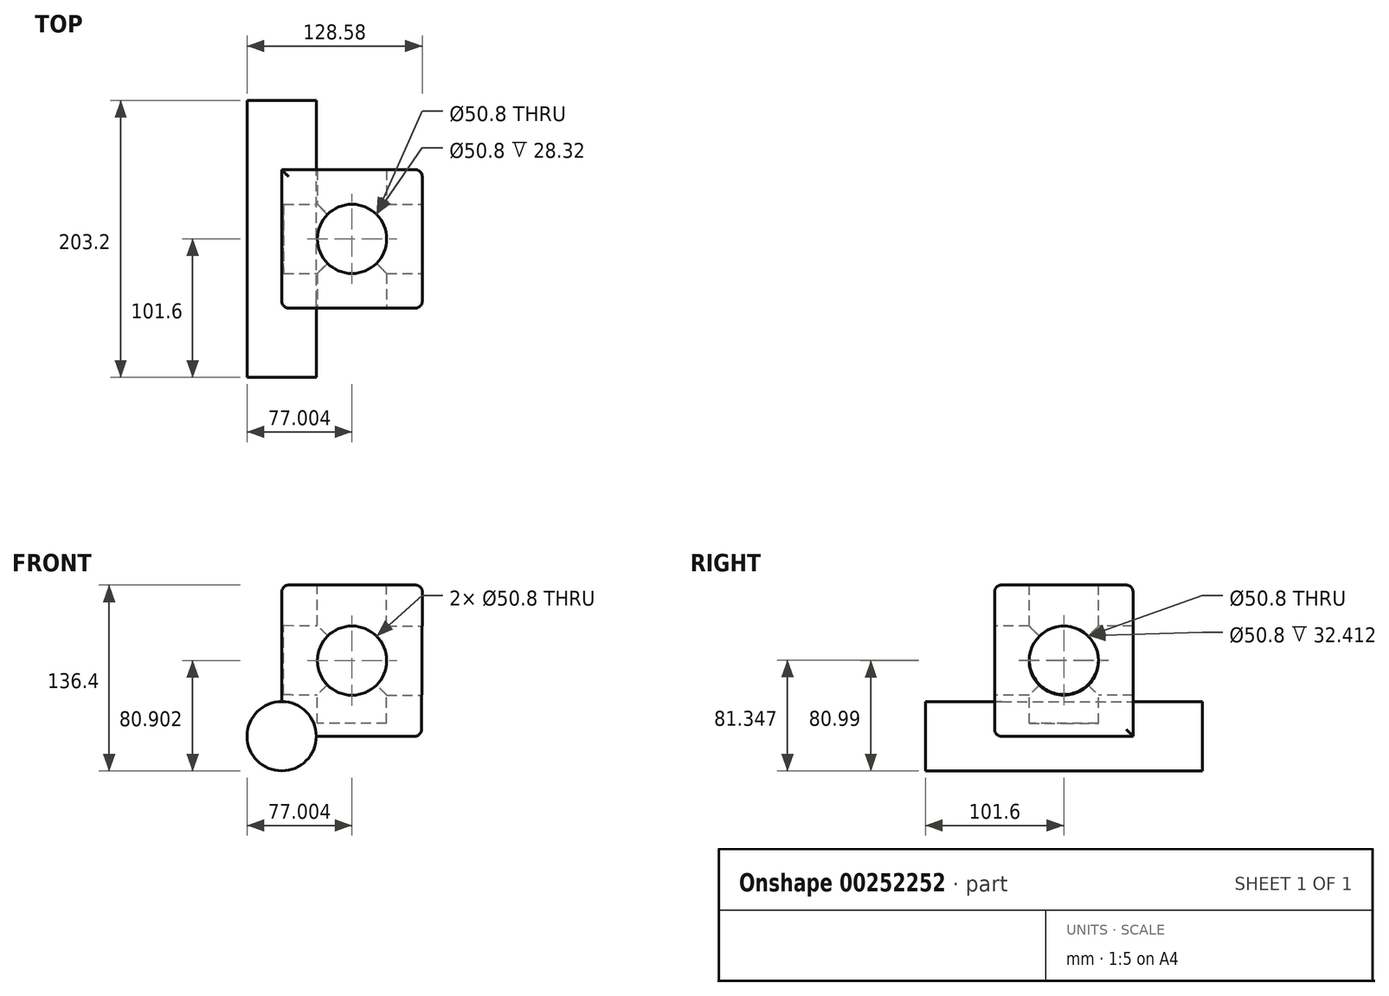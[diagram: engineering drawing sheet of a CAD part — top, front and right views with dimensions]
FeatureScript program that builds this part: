
annotation { "Feature Type Name" : "Feature", "Feature Type Description" : "" }
export const myFeature = defineFeature(function(context is Context, id is Id, definition is map)
    precondition{}
    {
        {
            var Q0;
            Q0=qCreatedBy(makeId("Front.planeOp"),FACE);
            var sketch = newSketch(context, id + "F0", { "sketchPlane" : qUnion([Q0])});
            skLineSegment(sketch, "E0", {"start": v(0, 0) * mm, "end": v(102.63, 0) * mm});
            skLineSegment(sketch, "E1", {"start": v(0, 0) * mm, "end": v(0, 111) * mm});
            skLineSegment(sketch, "E2", {"start": v(0, 111) * mm, "end": v(103.2, 111) * mm});
            skLineSegment(sketch, "E3", {"start": v(103.2, 111) * mm, "end": v(102.63, 0) * mm});
            skSolve(sketch);
        }
        {
            var Q0;
            Q0=makeQuery(id+"F0.imprint","IMPRINT",FACE,{"disambiguationData":[TD([[makeQuery(id+"F0.imprint","IMPRINT",EDGE,{"derivedFrom":sQuery(id+"F0.wireOp",EDGE,"E0")}),1.0]])]});
            extrude(context, id + "F1", {"entities" : qUnion([Q0]), "depth" : 101.6 * mm});
        }
        {
            var Q0;
            Q0=makeQuery(id+"F1.opExtrude","SWEPT_FACE",FACE,{"disambiguationData":[OSD([sQuery(id+"F0.wireOp",EDGE,"E2")])]});
            var sketch = newSketch(context, id + "F2", { "sketchPlane" : qUnion([Q0])});
            skPoint(sketch, "E4.start.orphan", {"position": v(51.6, 0) * mm});
            skCircle(sketch, "E5", {"center": v(51.6, -50.8) * mm, "radius": 25.4 * mm});
            skPoint(sketch, "E6.end.orphan", {"position": v(51.6, -101.6) * mm});
            skSolve(sketch);
        }
        {
            var Q0;
            Q0=makeQuery(id+"F2.imprint","IMPRINT",FACE,{"disambiguationData":[TD([[makeQuery(id+"F2.imprint","IMPRINT",EDGE,{"derivedFrom":sQuery(id+"F2.wireOp",EDGE,"E5")}),1.0]])]});
            extrude(context, id + "F3", {"entities" : qUnion([Q0]), "operationType" : NewBodyOperationType.REMOVE, "oppositeDirection" : true, "depth" : 101.6 * mm});
        }
        {
            var Q0;
            Q0=makeQuery(id+"F1.opExtrude","SWEPT_FACE",FACE,{"disambiguationData":[OSD([sQuery(id+"F0.wireOp",EDGE,"E3")])]});
            var sketch = newSketch(context, id + "F4", { "sketchPlane" : qUnion([Q0])});
            skCircle(sketch, "E7", {"center": v(-50.8, 56.04) * mm, "radius": 25.4 * mm});
            skPoint(sketch, "E8.orphan", {"position": v(-50.8, 111.54) * mm});
            skPoint(sketch, "E9.end.orphan", {"position": v(-50.8, 0.53) * mm});
            skSolve(sketch);
        }
        {
            var Q0;
            Q0=makeQuery(id+"F4.imprint","IMPRINT",FACE,{"disambiguationData":[TD([[makeQuery(id+"F4.imprint","IMPRINT",EDGE,{"derivedFrom":sQuery(id+"F4.wireOp",EDGE,"E7")}),1.0]])]});
            extrude(context, id + "F5", {"entities" : qUnion([Q0]), "operationType" : NewBodyOperationType.REMOVE, "oppositeDirection" : true, "depth" : 101.6 * mm});
        }
        {
            var Q0;
            Q0=makeQuery(id+"F1.opExtrude","CAP_FACE",FACE,{"disambiguationData":[OSD([sQuery(id+"F0.wireOp",EDGE,"E0"),sQuery(id+"F0.wireOp",EDGE,"E1"),sQuery(id+"F0.wireOp",EDGE,"E2"),sQuery(id+"F0.wireOp",EDGE,"E3")])],"isStart":false});
            var sketch = newSketch(context, id + "F6", { "sketchPlane" : qUnion([Q0])});
            skPoint(sketch, "E10.endSnap0", {"position": v(51.31, 0) * mm});
            skCircle(sketch, "E11", {"center": v(51.6, 55.5) * mm, "radius": 25.4 * mm});
            skPoint(sketch, "E12.orphan", {"position": v(51.6, 111) * mm});
            skPoint(sketch, "E10.end.orphan", {"position": v(51.6, 0) * mm});
            skSolve(sketch);
        }
        {
            var Q0;
            Q0=makeQuery(id+"F6.imprint","IMPRINT",FACE,{"disambiguationData":[TD([[makeQuery(id+"F6.imprint","IMPRINT",EDGE,{"derivedFrom":sQuery(id+"F6.wireOp",EDGE,"E11")}),1.0]])]});
            extrude(context, id + "F7", {"entities" : qUnion([Q0]), "operationType" : NewBodyOperationType.REMOVE, "oppositeDirection" : true, "depth" : 101.6 * mm});
        }
        {
            var Q0;
            Q0=makeQuery(id+"F1.opExtrude","SWEPT_EDGE",EDGE,{"disambiguationData":[OSD([sQuery(id+"F0.wireOp",EDGE,"E1"),sQuery(id+"F0.wireOp",EDGE,"E2")])]});
            var Q1;
            Q1=makeQuery(id+"F1.opExtrude","CAP_EDGE",EDGE,{"disambiguationData":[OSD([sQuery(id+"F0.wireOp",EDGE,"E2")])],"isStart":false});
            var Q2;
            Q2=makeQuery(id+"F1.opExtrude","SWEPT_EDGE",EDGE,{"disambiguationData":[OSD([sQuery(id+"F0.wireOp",EDGE,"E2"),sQuery(id+"F0.wireOp",EDGE,"E3")])]});
            var Q3;
            Q3=makeQuery(id+"F1.opExtrude","CAP_EDGE",EDGE,{"disambiguationData":[OSD([sQuery(id+"F0.wireOp",EDGE,"E2")])],"isStart":true});
            var Q4;
            Q4=makeQuery(id+"F1.opExtrude","CAP_EDGE",EDGE,{"disambiguationData":[OSD([sQuery(id+"F0.wireOp",EDGE,"E3")])],"isStart":true});
            var Q5;
            Q5=makeQuery(id+"F1.opExtrude","CAP_EDGE",EDGE,{"disambiguationData":[OSD([sQuery(id+"F0.wireOp",EDGE,"E3")])],"isStart":false});
            var Q6;
            Q6=makeQuery(id+"F1.opExtrude","SWEPT_EDGE",EDGE,{"disambiguationData":[OSD([sQuery(id+"F0.wireOp",EDGE,"E0"),sQuery(id+"F0.wireOp",EDGE,"E3")])]});
            var Q7;
            Q7=makeQuery(id+"F1.opExtrude","CAP_EDGE",EDGE,{"disambiguationData":[OSD([sQuery(id+"F0.wireOp",EDGE,"E0")])],"isStart":false});
            var Q8;
            Q8=makeQuery(id+"F1.opExtrude","CAP_EDGE",EDGE,{"disambiguationData":[OSD([sQuery(id+"F0.wireOp",EDGE,"E1")])],"isStart":false});
            fillet(context, id + "F8", {"entities" : qUnion([Q0, Q1, Q2, Q3, Q4, Q5, Q6, Q7, Q8]), "radius" : 5.08 * mm, "tangentPropagation" : true, "allowEdgeOverflow" : false});
        }
        {
            var Q0;
            Q0=qCreatedBy(makeId("Front.planeOp"),FACE);
            cPlane(context, id + "F9", {"entities" : qUnion([Q0]), "cplaneType" : CPlaneType.OFFSET, "offset" : 101.6 * mm, "width" : 152.4 * mm, "height" : 152.4 * mm});
        }
        {
            var Q0;
            Q0=qCreatedBy(id+"F9.planeOp",FACE);
            var sketch = newSketch(context, id + "F10", { "sketchPlane" : qUnion([Q0])});
            skCircle(sketch, "E13", {"center": v(0, 0) * mm, "radius": 25.4 * mm});
            skSolve(sketch);
        }
        {
            var Q0;
            Q0 = qSketchRegion(id + "F10", true);
            extrude(context, id + "F11", {"entities" : qUnion([Q0]), "operationType" : NewBodyOperationType.ADD, "depth" : 50.8 * mm, "hasSecondDirection" : true, "secondDirectionOppositeDirection" : true, "secondDirectionDepth" : 152.4 * mm});
        }
    });
